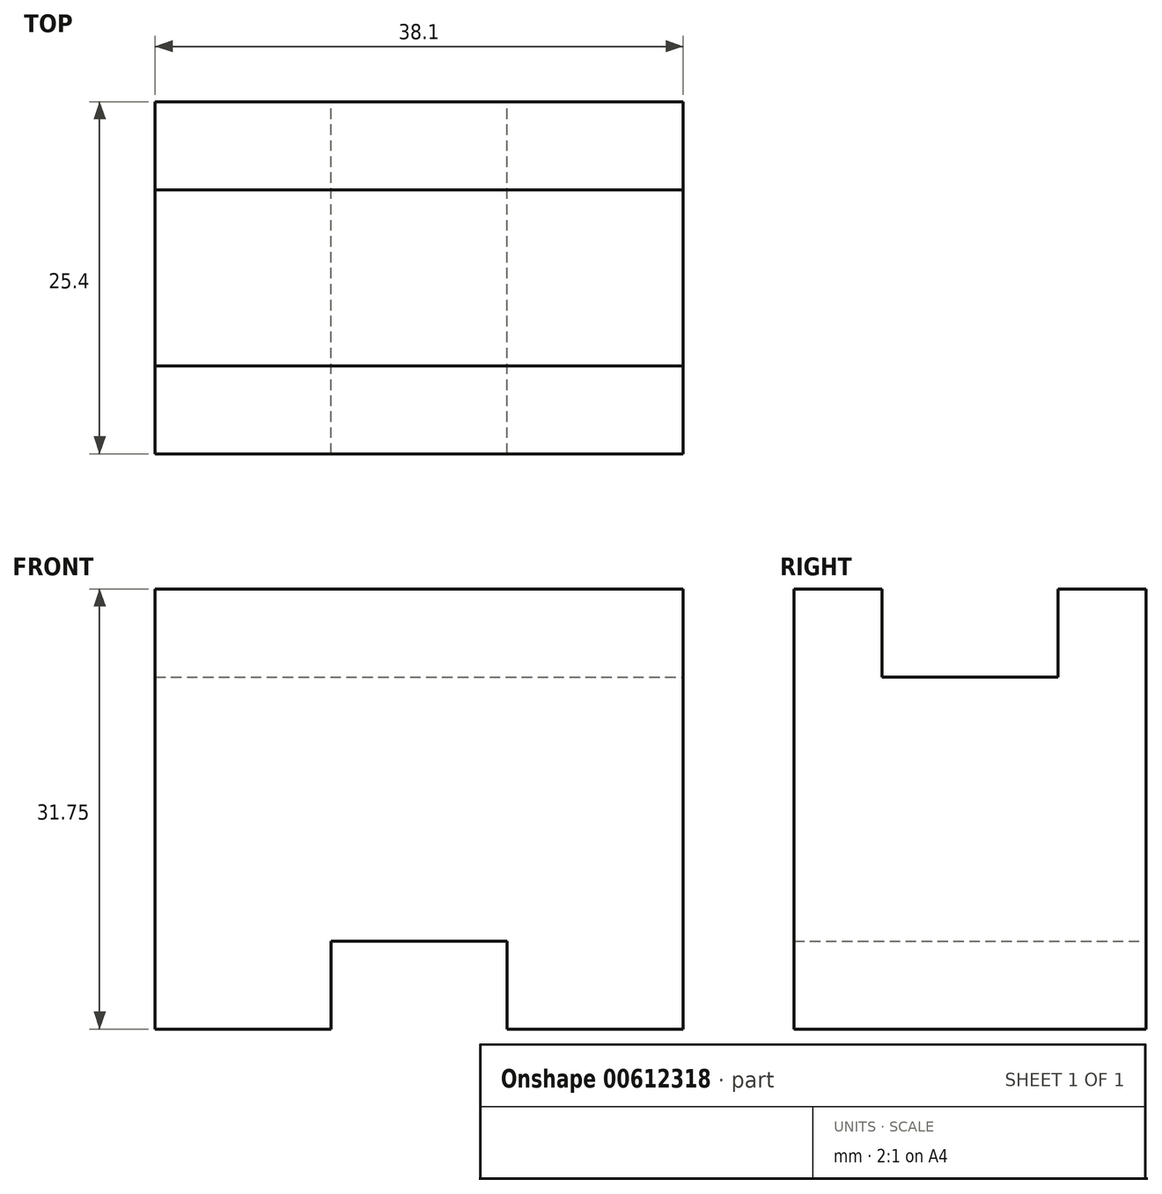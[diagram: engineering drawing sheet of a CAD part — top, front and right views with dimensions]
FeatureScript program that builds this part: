
annotation { "Feature Type Name" : "Feature", "Feature Type Description" : "" }
export const myFeature = defineFeature(function(context is Context, id is Id, definition is map)
    precondition{}
    {
        {
            var Q0;
            Q0=qCreatedBy(makeId("Front.planeOp"),FACE);
            var sketch = newSketch(context, id + "F0", { "sketchPlane" : qUnion([Q0])});
            skLineSegment(sketch, "E0", {"start": v(0, 0) * mm, "end": v(0, 31.75) * mm});
            skLineSegment(sketch, "E1", {"start": v(0, 31.75) * mm, "end": v(38.1, 31.75) * mm});
            skLineSegment(sketch, "E2", {"start": v(38.1, 31.75) * mm, "end": v(38.1, 0) * mm});
            skLineSegment(sketch, "E3", {"start": v(38.1, 0) * mm, "end": v(25.4, 0) * mm});
            skLineSegment(sketch, "E4", {"start": v(25.4, 0) * mm, "end": v(25.4, 6.35) * mm});
            skLineSegment(sketch, "E5", {"start": v(25.4, 6.35) * mm, "end": v(12.7, 6.35) * mm});
            skLineSegment(sketch, "E6", {"start": v(12.7, 6.35) * mm, "end": v(12.7, 0) * mm});
            skLineSegment(sketch, "E7", {"start": v(12.7, 0) * mm, "end": v(0, 0) * mm});
            skSolve(sketch);
        }
        {
            var Q0;
            Q0=qSketchRegion(id+"F0",true);
            var Q1;
            Q1=makeQuery(id+"F0.imprint","IMPRINT",FACE,{"disambiguationData":[TD([[makeQuery(id+"F0.imprint","IMPRINT",EDGE,{"derivedFrom":sQuery(id+"F0.wireOp",EDGE,"E0")}),-1.0]])]});
            extrude(context, id + "F1", {"entities" : qUnion([Q0, Q1]), "depth" : 25.4 * mm});
        }
        {
            var Q0;
            Q0=makeQuery(id+"F1.opExtrude","SWEPT_FACE",FACE,{"disambiguationData":[OSD([sQuery(id+"F0.wireOp",EDGE,"E1")])]});
            var sketch = newSketch(context, id + "F2", { "sketchPlane" : qUnion([Q0])});
            skLineSegment(sketch, "E8", {"start": v(0, -6.35) * mm, "end": v(38.1, -6.35) * mm});
            skLineSegment(sketch, "E9", {"start": v(38.1, -6.35) * mm, "end": v(38.1, -19.05) * mm});
            skLineSegment(sketch, "E10", {"start": v(38.1, -19.05) * mm, "end": v(0, -19.05) * mm});
            skLineSegment(sketch, "E11", {"start": v(0, -19.05) * mm, "end": v(0, -6.35) * mm});
            skLineSegment(sketch, "E12", {"start": v(0, 0) * mm, "end": v(0, -25.4) * mm});
            skLineSegment(sketch, "E13", {"start": v(0, -25.4) * mm, "end": v(38.1, -25.4) * mm});
            skLineSegment(sketch, "E14", {"start": v(38.1, -25.4) * mm, "end": v(38.1, 0) * mm});
            skLineSegment(sketch, "E15", {"start": v(38.1, 0) * mm, "end": v(0, 0) * mm});
            skSolve(sketch);
        }
        {
            var Q0;
            {var subQ0=sQuery(id+"F2.wireOp",EDGE,"E8");Q0=makeQuery(id+"F2.imprint","IMPRINT",FACE,{"disambiguationData":[TD([[makeQuery(id+"F2.imprint","IMPRINT",EDGE,{"derivedFrom":subQ0}),-1.0]])]});}
            extrude(context, id + "F3", {"entities" : qUnion([Q0]), "operationType" : NewBodyOperationType.REMOVE, "oppositeDirection" : true, "depth" : 6.35 * mm});
        }
    });
